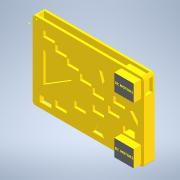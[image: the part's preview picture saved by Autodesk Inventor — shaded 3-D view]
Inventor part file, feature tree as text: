
AUTODESK INVENTOR PART (.ipt)
format: ipt  version: 2021 (Build 250183000, 183)  size: 283,648 bytes
history: native  units: mm
features: sketch x13, extrude x9, hole x2, fillet x1
ambient origin geometry x8: Origin, YZ Plane, XZ Plane, XY Plane, X Axis, Y Axis, Z Axis, Center Point
bodies: Solid1 (feature_tree)
feature tree (25):
  extrude  "Extrusion1"  Depth=216.0mm
  fillet  "Fillet1"  Radius=30.0mm
  hole  "Hole1"  [1 undecoded]
  hole  "Hole2"  [1 undecoded]
  extrude  "Extrusion2"  Depth=8.0mm TaperAngle=0.0deg
  extrude  "Extrusion3"  Depth=10.0mm TaperAngle=0.0deg
  extrude  "Extrusion4"  Depth=20.0mm TaperAngle=0.0deg
  extrude  "Extrusion5"  Depth=216.0mm TaperAngle=0.0deg
  sketch  "Sketch8"  dims[d29=50.0mm d30=0.0mm d31=20.0mm d32=23.0mm d33=0.0mm d34=0.0mm]
  extrude  "Extrusion6"  [1 undecoded]
  sketch  "Sketch10"  dims[d39=216.0mm d40=0.0mm]
  extrude  "Extrusion7"  [1 undecoded]
  extrude  "Extrusion8"  [1 undecoded]
  extrude  "Extrusion9"  [1 undecoded]
  sketch  "Sketch1"  dims[d0=310.0mm d1=216.0mm d2=30.0mm d3=0.0mm]
  sketch  "Sketch2"  dims[d4=8.0mm d5=15.0mm]
  sketch  "Sketch3"  dims[d6=15.0mm]
  sketch  "Sketch4"  dims[d7=4.0mm d8=6.0mm d9=4.0mm d10=2.0mm d11=90.0deg d12=8.0mm d13=20.594885mm d14=15.0mm]
  sketch  "Sketch5"  dims[d15=15.0mm]
  sketch  "Sketch6"  dims[d16=4.0mm d17=6.0mm d18=4.0mm d19=2.0mm d20=90.0deg d21=8.0mm d22=20.594885mm d23=230.0mm d24=0.0mm]
  sketch  "Sketch7"  dims[d25=10.0mm d26=0.0mm d27=10.0mm d28=0.0mm]
  sketch  "Sketch9"  dims[d35=220.0mm d36=0.0mm d37=216.0mm d38=0.0mm]
  sketch  "Sketch11"
  sketch  "Sketch12"
  sketch  "Sketch13"
note: 6 required parameter values undecoded (feature->parameter linkage not recoverable at this tier; creation-order binding heuristic only, values carry confidence <= 0.55)
